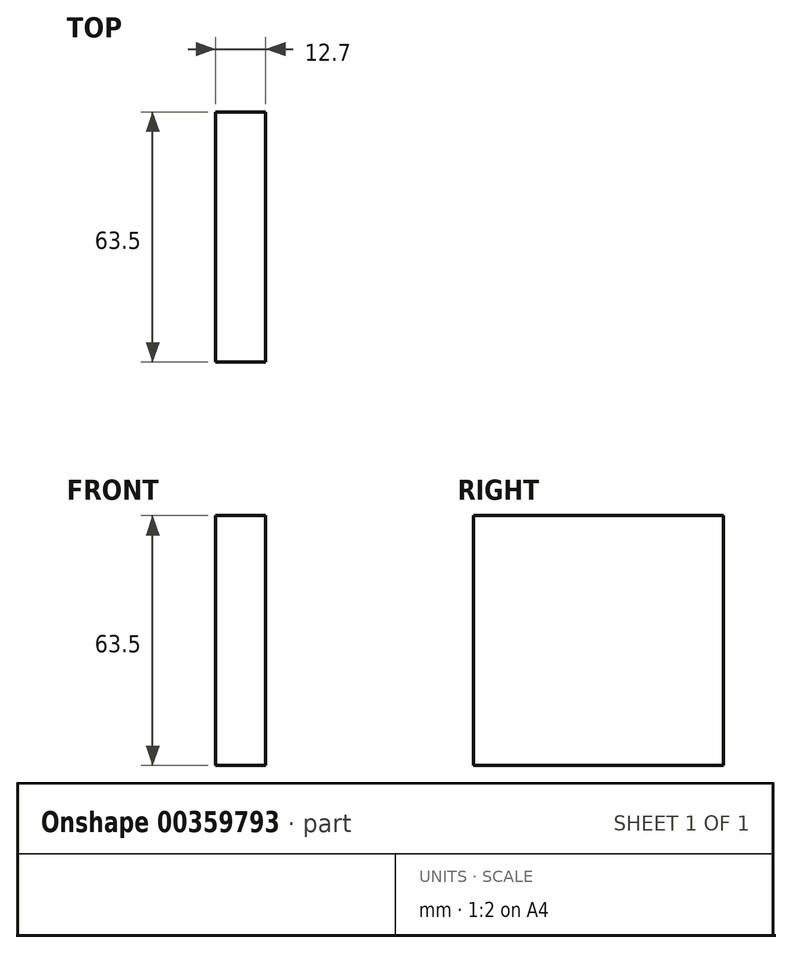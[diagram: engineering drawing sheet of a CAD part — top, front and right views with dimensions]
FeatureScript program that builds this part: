
annotation { "Feature Type Name" : "Feature", "Feature Type Description" : "" }
export const myFeature = defineFeature(function(context is Context, id is Id, definition is map)
    precondition{}
    {
        {
            var Q0;
            Q0=qCreatedBy(makeId("Front.planeOp"),FACE);
            var sketch = newSketch(context, id + "F0", { "sketchPlane" : qUnion([Q0])});
            skLineSegment(sketch, "E0.bottom", {"start": v(0, 0) * mm, "end": v(12.7, 0) * mm});
            skLineSegment(sketch, "E0.top", {"start": v(0, -63.5) * mm, "end": v(12.7, -63.5) * mm});
            skLineSegment(sketch, "E0.left", {"start": v(0, 0) * mm, "end": v(0, -63.5) * mm});
            skLineSegment(sketch, "E0.right", {"start": v(12.7, 0) * mm, "end": v(12.7, -63.5) * mm});
            skSolve(sketch);
        }
        {
            var Q0;
            Q0 = qSketchRegion(id + "F0", true);
            extrude(context, id + "F1", {"entities" : qUnion([Q0]), "depth" : 63.5 * mm});
        }
    });
